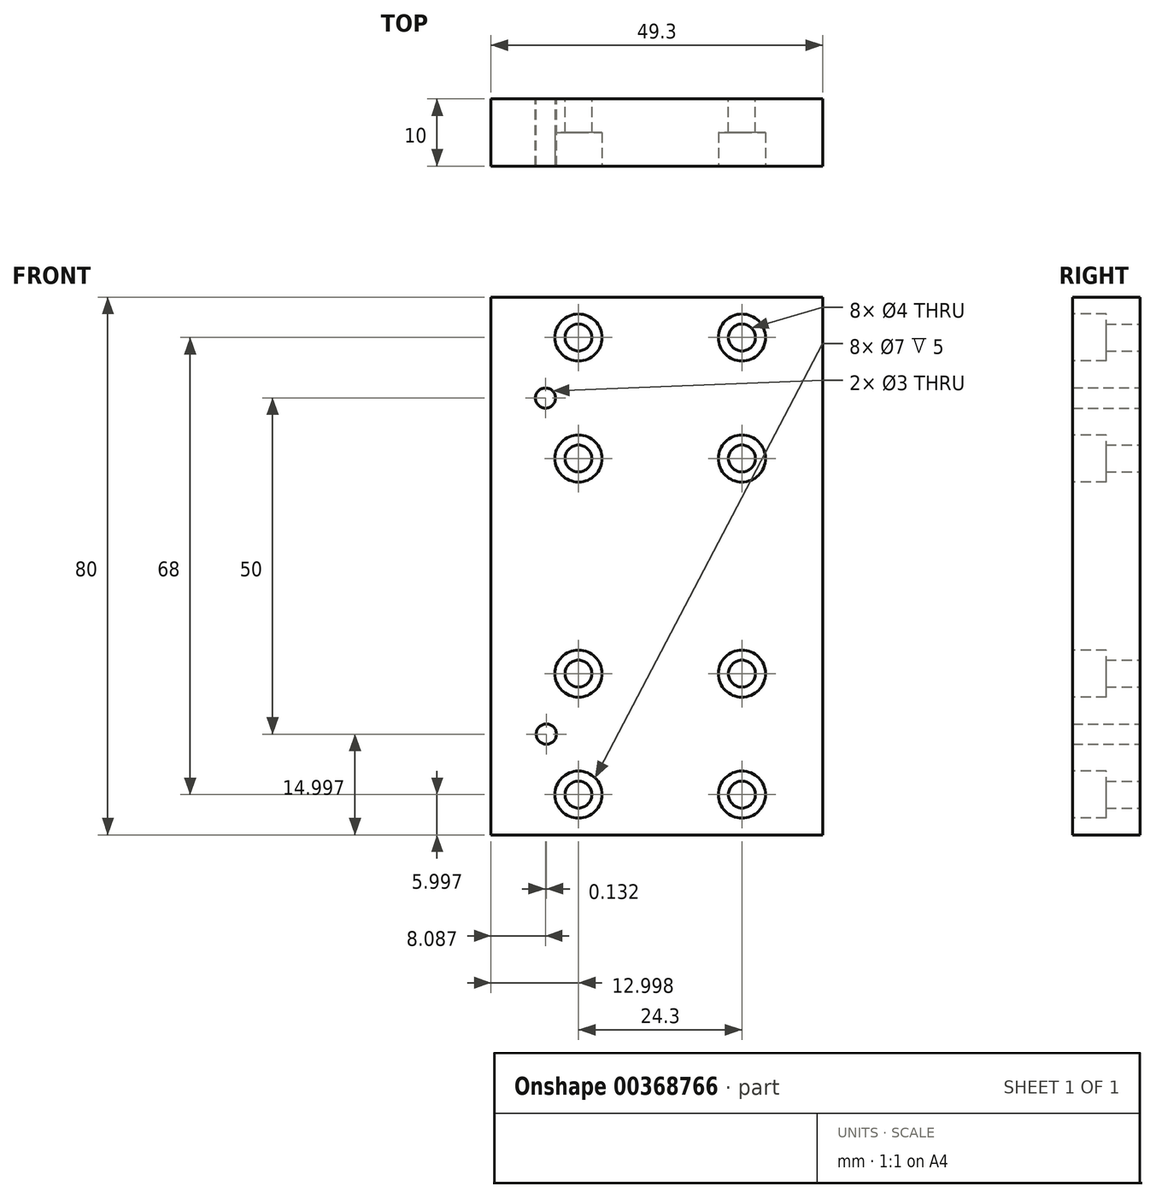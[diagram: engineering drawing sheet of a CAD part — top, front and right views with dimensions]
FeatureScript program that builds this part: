
annotation { "Feature Type Name" : "Feature", "Feature Type Description" : "" }
export const myFeature = defineFeature(function(context is Context, id is Id, definition is map)
    precondition{}
    {
        {
            var Q0;
            Q0=qCreatedBy(makeId("Front.planeOp"),FACE);
            var sketch = newSketch(context, id + "F0", { "sketchPlane" : qUnion([Q0])});
            skLineSegment(sketch, "E0.bottom", {"start": v(-100.95, 138.47) * mm, "end": v(-150.25, 138.47) * mm});
            skLineSegment(sketch, "E0.top", {"start": v(-100.95, 58.47) * mm, "end": v(-150.25, 58.47) * mm});
            skLineSegment(sketch, "E0.left", {"start": v(-100.95, 138.47) * mm, "end": v(-100.95, 58.47) * mm});
            skLineSegment(sketch, "E0.right", {"start": v(-150.25, 138.47) * mm, "end": v(-150.25, 58.47) * mm});
            skCircle(sketch, "E1", {"center": v(-112.95, 107.25) * mm, "radius": 2 * mm});
            skCircle(sketch, "E2", {"center": v(-112.95, 89.25) * mm, "radius": 2 * mm});
            skCircle(sketch, "E3", {"center": v(-137.25, 89.25) * mm, "radius": 2 * mm});
            skCircle(sketch, "E4", {"center": v(-137.25, 107.25) * mm, "radius": 2 * mm});
            skCircle(sketch, "E5", {"center": v(-142.16, 123.47) * mm, "radius": 1.5 * mm});
            skCircle(sketch, "E6", {"center": v(-142.03, 73.47) * mm, "radius": 1.5 * mm});
            skLineSegment(sketch, "E7", {"start": v(-137.25, 107.25) * mm, "end": v(-137.25, 89.25) * mm, "construction": true});
            skLineSegment(sketch, "E8", {"start": v(-137.25, 89.25) * mm, "end": v(-112.95, 89.25) * mm, "construction": true});
            skLineSegment(sketch, "E9", {"start": v(-112.95, 107.25) * mm, "end": v(-137.25, 107.25) * mm, "construction": true});
            skLineSegment(sketch, "E10", {"start": v(-112.95, 107.25) * mm, "end": v(-112.95, 89.25) * mm, "construction": true});
            skCircle(sketch, "E11", {"center": v(-112.95, 82.47) * mm, "radius": 2 * mm});
            skCircle(sketch, "E12", {"center": v(-112.95, 64.47) * mm, "radius": 2 * mm});
            skCircle(sketch, "E13", {"center": v(-137.25, 64.47) * mm, "radius": 2 * mm});
            skCircle(sketch, "E14", {"center": v(-137.25, 82.47) * mm, "radius": 2 * mm});
            skLineSegment(sketch, "E15", {"start": v(-137.25, 82.47) * mm, "end": v(-137.25, 64.47) * mm, "construction": true});
            skLineSegment(sketch, "E16", {"start": v(-137.25, 64.47) * mm, "end": v(-112.95, 64.47) * mm, "construction": true});
            skLineSegment(sketch, "E17", {"start": v(-112.95, 82.47) * mm, "end": v(-137.25, 82.47) * mm, "construction": true});
            skLineSegment(sketch, "E18", {"start": v(-112.95, 82.47) * mm, "end": v(-112.95, 64.47) * mm, "construction": true});
            skCircle(sketch, "E19", {"center": v(-112.95, 132.47) * mm, "radius": 2 * mm});
            skCircle(sketch, "E20", {"center": v(-112.95, 114.47) * mm, "radius": 2 * mm});
            skCircle(sketch, "E21", {"center": v(-137.25, 114.47) * mm, "radius": 2 * mm});
            skCircle(sketch, "E22", {"center": v(-137.25, 132.47) * mm, "radius": 2 * mm});
            skLineSegment(sketch, "E23", {"start": v(-137.25, 132.47) * mm, "end": v(-137.25, 114.47) * mm, "construction": true});
            skLineSegment(sketch, "E24", {"start": v(-137.25, 114.47) * mm, "end": v(-112.95, 114.47) * mm, "construction": true});
            skLineSegment(sketch, "E25", {"start": v(-112.95, 132.47) * mm, "end": v(-137.25, 132.47) * mm, "construction": true});
            skLineSegment(sketch, "E26", {"start": v(-112.95, 132.47) * mm, "end": v(-112.95, 114.47) * mm, "construction": true});
            skPoint(sketch, "E27", {"position": v(-137.25, 98.25) * mm});
            skPoint(sketch, "E28", {"position": v(-137.25, 123.47) * mm});
            skPoint(sketch, "E29", {"position": v(-137.25, 73.47) * mm});
            skSolve(sketch);
        }
        {
            var Q0;
            Q0=makeQuery(id+"F0.imprint","IMPRINT",FACE,{"disambiguationData":[TD([[makeQuery(id+"F0.imprint","IMPRINT",EDGE,{"derivedFrom":sQuery(id+"F0.wireOp",EDGE,"E4")}),1.0]])]});
            var Q1;
            Q1=makeQuery(id+"F0.imprint","IMPRINT",FACE,{"disambiguationData":[TD([[makeQuery(id+"F0.imprint","IMPRINT",EDGE,{"derivedFrom":sQuery(id+"F0.wireOp",EDGE,"E1")}),1.0]])]});
            var Q2;
            Q2=makeQuery(id+"F0.imprint","IMPRINT",FACE,{"disambiguationData":[TD([[makeQuery(id+"F0.imprint","IMPRINT",EDGE,{"derivedFrom":sQuery(id+"F0.wireOp",EDGE,"E0.bottom")}),1.0]])]});
            var Q3;
            Q3=makeQuery(id+"F0.imprint","IMPRINT",FACE,{"disambiguationData":[TD([[makeQuery(id+"F0.imprint","IMPRINT",EDGE,{"derivedFrom":sQuery(id+"F0.wireOp",EDGE,"E3")}),1.0]])]});
            var Q4;
            Q4=makeQuery(id+"F0.imprint","IMPRINT",FACE,{"disambiguationData":[TD([[makeQuery(id+"F0.imprint","IMPRINT",EDGE,{"derivedFrom":sQuery(id+"F0.wireOp",EDGE,"E2")}),1.0]])]});
            extrude(context, id + "F1", {"entities" : qUnion([Q0, Q1, Q2, Q3, Q4]), "depth" : 10 * mm, "offsetDistance" : 25 * mm});
        }
        {
            var Q0;
            Q0=makeQuery(id+"F1.opExtrude","CAP_FACE",FACE,{"disambiguationData":[OSD([sQuery(id+"F0.wireOp",EDGE,"E0.bottom"),sQuery(id+"F0.wireOp",EDGE,"E0.top"),sQuery(id+"F0.wireOp",EDGE,"E0.left"),sQuery(id+"F0.wireOp",EDGE,"E0.right"),sQuery(id+"F0.wireOp",EDGE,"E1"),sQuery(id+"F0.wireOp",EDGE,"E2"),sQuery(id+"F0.wireOp",EDGE,"E3"),sQuery(id+"F0.wireOp",EDGE,"E4"),sQuery(id+"F0.wireOp",EDGE,"E5"),sQuery(id+"F0.wireOp",EDGE,"E6"),sQuery(id+"F0.wireOp",EDGE,"E11"),sQuery(id+"F0.wireOp",EDGE,"E12"),sQuery(id+"F0.wireOp",EDGE,"E13"),sQuery(id+"F0.wireOp",EDGE,"E14"),sQuery(id+"F0.wireOp",EDGE,"E19"),sQuery(id+"F0.wireOp",EDGE,"E20"),sQuery(id+"F0.wireOp",EDGE,"E21"),sQuery(id+"F0.wireOp",EDGE,"E22")])],"isStart":false});
            var sketch = newSketch(context, id + "F2", { "sketchPlane" : qUnion([Q0])});
            skCircle(sketch, "E30", {"center": v(-137.25, 132.47) * mm, "radius": 3.5 * mm});
            skCircle(sketch, "E31", {"center": v(-112.95, 132.47) * mm, "radius": 3.5 * mm});
            skCircle(sketch, "E32", {"center": v(-112.95, 114.47) * mm, "radius": 3.5 * mm});
            skCircle(sketch, "E33", {"center": v(-137.25, 114.47) * mm, "radius": 3.5 * mm});
            skCircle(sketch, "E34", {"center": v(-137.25, 82.47) * mm, "radius": 3.5 * mm});
            skCircle(sketch, "E35", {"center": v(-112.95, 82.47) * mm, "radius": 3.5 * mm});
            skCircle(sketch, "E36", {"center": v(-112.95, 64.47) * mm, "radius": 3.5 * mm});
            skCircle(sketch, "E37", {"center": v(-137.25, 64.47) * mm, "radius": 3.5 * mm});
            skSolve(sketch);
        }
        {
            var Q0;
            Q0 = qSketchRegion(id + "F2", true);
            extrude(context, id + "F3", {"entities" : qUnion([Q0]), "operationType" : NewBodyOperationType.REMOVE, "oppositeDirection" : true, "depth" : 5 * mm, "offsetDistance" : 25 * mm});
        }
    });
